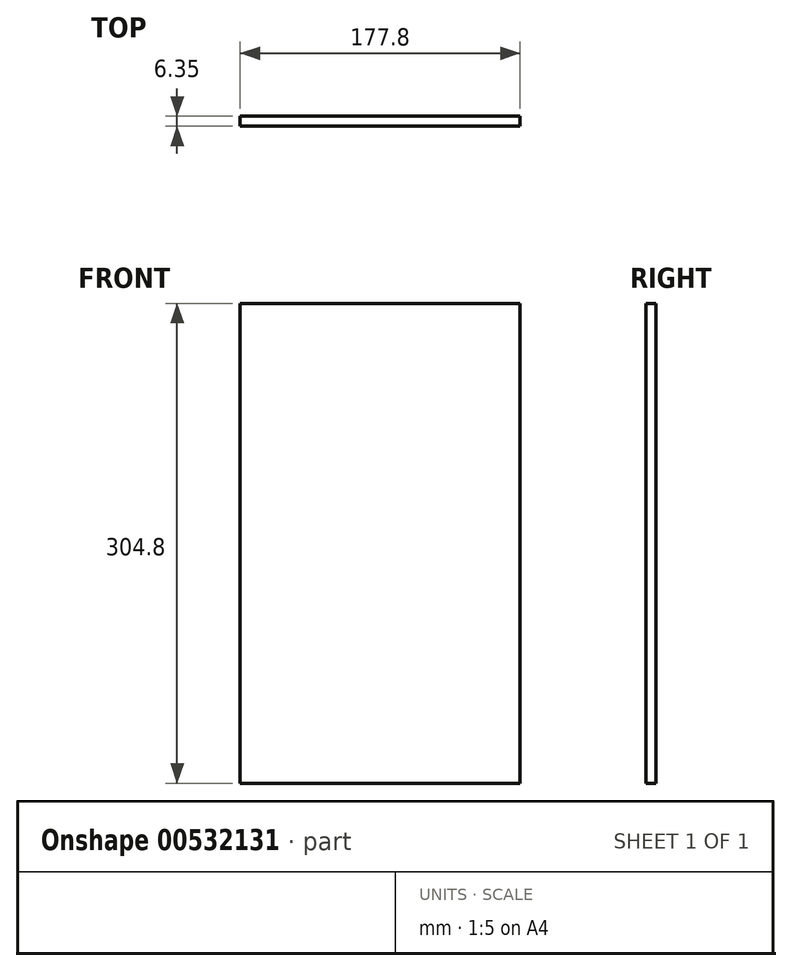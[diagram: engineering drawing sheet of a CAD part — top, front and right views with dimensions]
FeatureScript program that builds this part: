
annotation { "Feature Type Name" : "Feature", "Feature Type Description" : "" }
export const myFeature = defineFeature(function(context is Context, id is Id, definition is map)
    precondition{}
    {
        {
            var Q0;
            Q0=qCreatedBy(makeId("Front.planeOp"),FACE);
            var sketch = newSketch(context, id + "F0", { "sketchPlane" : qUnion([Q0])});
            skLineSegment(sketch, "E0.bottom", {"start": v(88.9, -152.4) * mm, "end": v(-88.9, -152.4) * mm});
            skLineSegment(sketch, "E0.top", {"start": v(88.9, 152.4) * mm, "end": v(-88.9, 152.4) * mm});
            skLineSegment(sketch, "E0.left", {"start": v(88.9, -152.4) * mm, "end": v(88.9, 152.4) * mm});
            skLineSegment(sketch, "E0.right", {"start": v(-88.9, -152.4) * mm, "end": v(-88.9, 152.4) * mm});
            skPoint(sketch, "E0.middle", {"position": v(0, 0) * mm});
            skSolve(sketch);
        }
        {
            var Q0;
            Q0=qSketchRegion(id+"F0",true);
            extrude(context, id + "F1", {"entities" : qUnion([Q0]), "depth" : 6.35 * mm, "offsetDistance" : 25.4 * mm});
        }
    });
